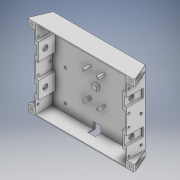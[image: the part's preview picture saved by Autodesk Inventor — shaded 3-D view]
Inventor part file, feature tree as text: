
AUTODESK INVENTOR PART (.ipt)
format: ipt  version: 2022 (Build 260153000, 153)  size: 629,248 bytes
history: native  units: in
note: dims shown in document units (in); Inventor stores cm internally (conversion verified against a paired STEP export)
features: sketch x22, extrude x20, projected_geometry x9, plane x1
ambient origin geometry x8: Origin, YZ Plane, XZ Plane, XY Plane, X Axis, Y Axis, Z Axis, Center Point
bodies: Solid1 (feature_tree)
feature tree (52):
  sketch  "Sketch1"  dims[d0=4.6528in d1=4.0681in]
  sketch  "Sketch2"  dims[d2=0.9449in d3=0.0in d4=0.1008in d5=0.0in]
  extrude  "Extrusion1"  Depth=4.0681in
  extrude  "Extrusion2"  Depth=0.1008in TaperAngle=0.0deg
  extrude  "Extrusion3"  Depth=4.1732in TaperAngle=0.0deg
  extrude  "Extrusion4"  Depth=0.252in
  extrude  "Extrusion5"  Depth=0.252in
  extrude  "Extrusion6"  Depth=0.3543in TaperAngle=0.0deg
  plane  "Work Plane1"
  sketch  "Sketch7"  dims[d18=0.537in d21=0.7311in]
  sketch  "Sketch8"  dims[d23=0.2756in d24=0.4528in]
  extrude  "Extrusion8"  Depth=0.7311in
  sketch  "Sketch10"  dims[d31=0.9449in d32=0.0in d33=0.8441in d34=0.0in]
  extrude  "Extrusion9"  Depth=0.4528in
  extrude  "Extrusion10"  Depth=0.8819in
  extrude  "Extrusion11"  Depth=0.8441in TaperAngle=0.0deg
  extrude  "Extrusion12"  Depth=0.8441in
  sketch  "Sketch13"  dims[d45=0.2184in d46=0.0in d47=0.7087in]
  extrude  "Extrusion13"  Depth=5.7809in TaperAngle=0.0deg
  extrude  "Extrusion14"  Depth=0.7087in
  extrude  "Extrusion15"  Depth=0.3434in TaperAngle=0.0deg
  extrude  "Extrusion16"  Depth=0.1575in
  extrude  "Extrusion17"  Depth=0.1299in
  extrude  "Extrusion18"  Depth=0.1102in
  extrude  "Extrusion19"  Depth=0.1299in
  sketch  "Sketch19"  dims[d62=0.1102in d63=0.1299in d64=0.1299in d65=0.1102in d66=0.1299in d67=0.1299in]
  extrude  "Extrusion21"  Depth=0.1102in
  extrude  "Extrusion22"  Depth=5.5049in TaperAngle=0.0deg
  sketch  "Sketch23"  dims[d79=0.1919in d80=0.1919in d81=0.3937in d82=0.0in d85=0.8563in d86=0.0in d89=0.8441in d90=0.0in d91=0.0591in d92=29.9066in d93=0.0in d94=1.6434in d95=0.4818in d96=2.0826in d97=3.6914in]
  sketch  "Sketch3"  dims[d6=0.1008in d7=0.0in d8=4.1732in d9=0.0in]
  sketch  "Sketch4"  dims[d10=0.0512in d11=0.252in]
  sketch  "Sketch5"  dims[d12=0.0512in d13=0.252in]
  sketch  "Sketch6"  dims[d14=0.3543in d15=0.0in d16=0.3543in d17=0.0in]
  projected_geometry  "Projected Loop1"
  projected_geometry  "Projected Loop2"
  projected_geometry  "Projected Loop3"
  sketch  "Sketch9"  dims[d29=0.3063in d30=0.8819in]
  projected_geometry  "Projected Loop4"
  sketch  "Sketch11"  dims[d35=0.8441in d36=0.0in d37=0.2776in]
  sketch  "Sketch12"  dims[d38=0.2776in d43=5.7809in d44=0.0in]
  projected_geometry  "Projected Loop5"
  sketch  "Sketch14"  dims[d48=1.4016in d51=0.3434in d52=0.0in]
  projected_geometry  "Projected Loop6"
  projected_geometry  "Projected Loop7"
  sketch  "Sketch15"  dims[d53=0.1575in d54=0.0in d55=0.1299in]
  sketch  "Sketch16"  dims[d56=0.1299in d57=0.1299in]
  projected_geometry  "Projected Loop8"
  sketch  "Sketch17"  dims[d58=0.0in d59=0.1102in]
  sketch  "Sketch18"  dims[d60=0.1299in d61=0.1299in]
  sketch  "Sketch20"  dims[d68=0.1102in d71=5.5049in d72=0.0in]
  sketch  "Sketch21"  dims[d73=0.1826in d74=0.0in]
  projected_geometry  "Projected Loop10"
